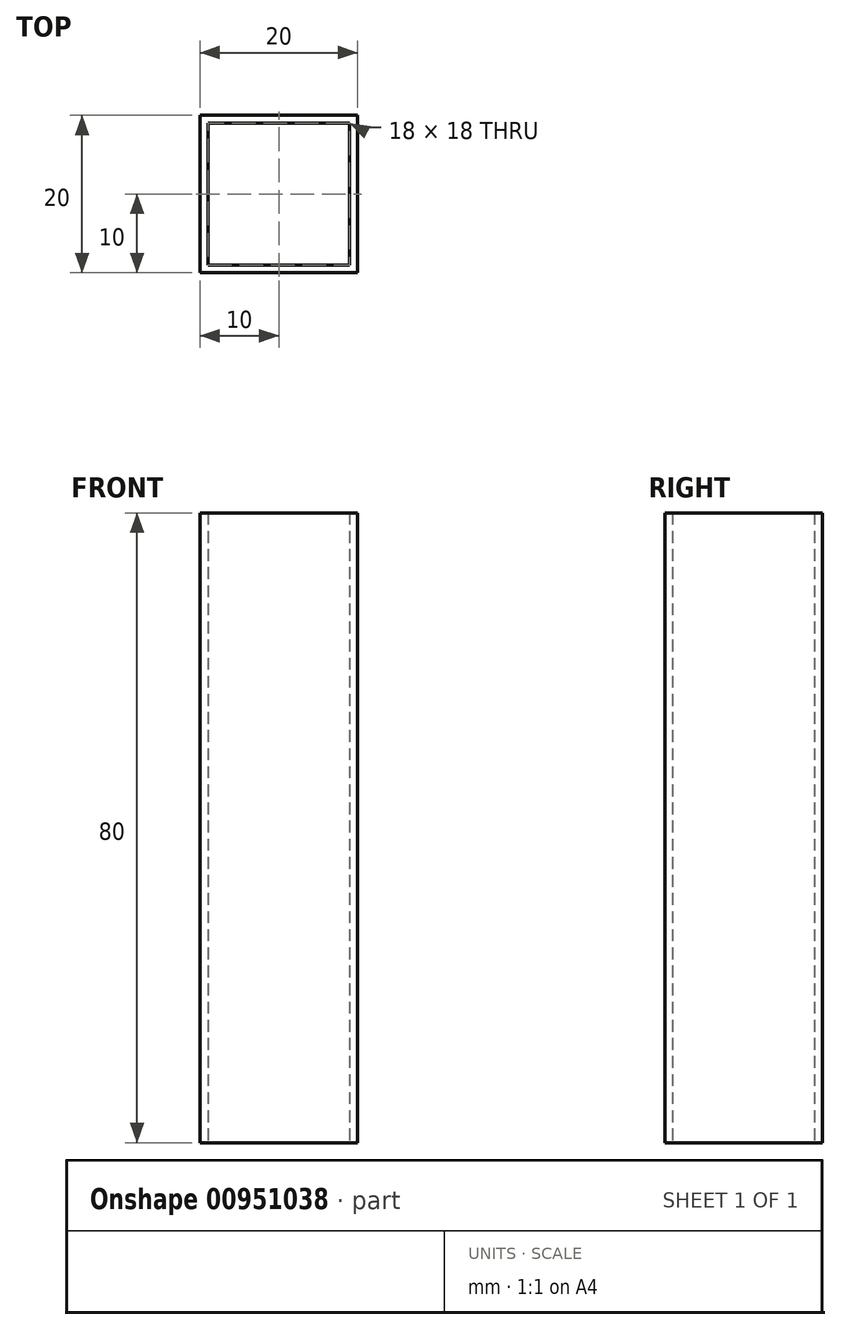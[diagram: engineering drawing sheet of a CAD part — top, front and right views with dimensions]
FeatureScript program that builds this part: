
annotation { "Feature Type Name" : "Feature", "Feature Type Description" : "" }
export const myFeature = defineFeature(function(context is Context, id is Id, definition is map)
    precondition{}
    {
        {
            var Q0;
            Q0=qCreatedBy(makeId("Top.planeOp"),FACE);
            var sketch = newSketch(context, id + "F0", { "sketchPlane" : qUnion([Q0])});
            skLineSegment(sketch, "E0.bottom", {"start": v(10, 10) * mm, "end": v(-10, 10) * mm});
            skLineSegment(sketch, "E0.top", {"start": v(10, -10) * mm, "end": v(-10, -10) * mm});
            skLineSegment(sketch, "E0.left", {"start": v(10, 10) * mm, "end": v(10, -10) * mm});
            skLineSegment(sketch, "E0.right", {"start": v(-10, 10) * mm, "end": v(-10, -10) * mm});
            skPoint(sketch, "E0.middle", {"position": v(0, 0) * mm});
            skLineSegment(sketch, "E1.bottom", {"start": v(9, 9) * mm, "end": v(-9, 9) * mm});
            skLineSegment(sketch, "E1.top", {"start": v(9, -9) * mm, "end": v(-9, -9) * mm});
            skLineSegment(sketch, "E1.left", {"start": v(9, 9) * mm, "end": v(9, -9) * mm});
            skLineSegment(sketch, "E1.right", {"start": v(-9, 9) * mm, "end": v(-9, -9) * mm});
            skSolve(sketch);
        }
        {
            var Q0;
            Q0=makeQuery(id+"F0.imprint","IMPRINT",FACE,{"disambiguationData":[TD([[makeQuery(id+"F0.imprint","IMPRINT",EDGE,{"derivedFrom":sQuery(id+"F0.wireOp",EDGE,"E0.bottom")}),1.0]])]});
            extrude(context, id + "F1", {"entities" : qUnion([Q0]), "depth" : 80 * mm, "offsetDistance" : 25 * mm});
        }
    });
